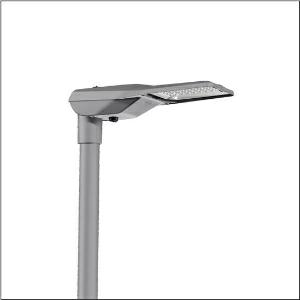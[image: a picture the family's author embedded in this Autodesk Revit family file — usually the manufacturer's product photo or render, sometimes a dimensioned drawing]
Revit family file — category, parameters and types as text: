
# Revit family: streetlight_sl_21_iq_mini___stw1_0a_5xe2e31y08hb_518f
name_source: partatom
category: Lighting Fixtures
units: mm (PartAtom-declared; Revit-internal decimal feet)

## family parameters
Cut with Voids When Loaded = No
Host = Face
Light Source = No
Part Type = Normal
Room Calculation Point = No
Round Connector Dimension = Use Diameter
Shared = No

## types (1)
- --- (1 x LED, 9750 lm, 71 W, 3000K)
    Apparent Load = 71 VA
    CIE Flux Codes = 38 75 98 100 100
    Color Rendering = 70
    Color Temperature = 3000K
    Default Elevation = 1800 mm
    Description = Streetlight SL 21 iQ mini, mast luminaire, primary light control with lens, of PMMA, primary optical cover: cover, of toughened safety glass, transparent, light distribution: STW1.0a, light emission: direct distribution, primary light characteristic: asymmetric, installation type: post-top, side-entry, LED, High Power LED, rated luminous flux: 9.750lm, luminous efficacy: 137lm/W, light colour: 730, colour temperature: 3000K, control: presetting dimming logarithmic, Street-Remote, Auto-Match, Temp-Guard, Lumen-Switch, Night-Set, Smart-Wire, Light-Fading, Desk-Remote (wireless, voltage-free reading and setting of iQ features in the workshop via application-optimized NFC function/RFID function), optimised constant luminous flux control (CLO 2.0), mains connection: 220..240V, AC, 50/60Hz, start of lifetime: 71W, end of service life: 75W, reduction: 30W, luminaire housing, of diecast aluminium, powder-coated, Siteco® metallic grey (DB 702S), corrosivity category C5 mid according to DIN EN ISO 12944, please order mast flange separately, inclination adjustable: 0°, 5°, 10°, 15°, sealing non-destructively replaceable, multi-level sealing system, length: 628mm, width: 235mm, height: 110mm, mast flange for spigot size: 42mm (side-entry): 5XC10008XM4, 60/48mm (side-entry/post-top): 5XC10108XM2, 76/60mm (side-entry/post-top): 5XC10108XM1, Smart Interface below and above, protection rating (complete): IP66, insulation class (complete): insulation class II (safety insulation), certification: CE, ENEC, ENEC+, VDE, impact resistance: IK09, permissible operating ambient temperature for outdoor applications: -40..+50°C, standard-compliant lighting for roads and squares, packaging unit: 1 piece

Light Distribution: STW1.0a
    Height = 110 mm
    Lamp = 1 x LED
    Lamp Light Flux = 9750 lm
    Lamp Power = 71 W
    Lamp count = 1
    Length = 625 mm
    Luminous efficacy = 137 lm/W
    Manufacturer = Siteco
    ModVariant = No
    Model = 5XE2E31Y08HB
    Number of Poles = 1
    OnlyDefault = Yes
    Power Factor = 1
    Product Name = Streetlight SL 21 iQ mini | STW1.0a
    Product group = mast luminaire | pylon top
    ProductGroupID = 6100
    Protection Class = Protection class II
    Protection Degree = IP 66
    RLX_Detail_Level = 1
    RLX_Emergency_Light_Flux = 0 lm
    RLX_Emergency_Type = 0
    RLX_Emergency_Type_DB = No
    RlxData = <blob elided: 92717 chars, md5=68204dd1>
    Socket = socket
    Standby Power = 0 W
    System Light Flux = 9750 lm
    System Power = 71 W
    Type Comments = factory setting: luminous flux: 100 % | dim-lin: 254 | 716 mA
    Type Image = l_1003514.jpg
    URL = http://relux.com
    VarID = @adj_044339
    Voltage = 0 V
    Weight = 0.00 kg
    Width = 234 mm

## geometry (parser evidence)
native form markers: Blend x4, Sweep x11
no freeform markers — native parametric forms only
